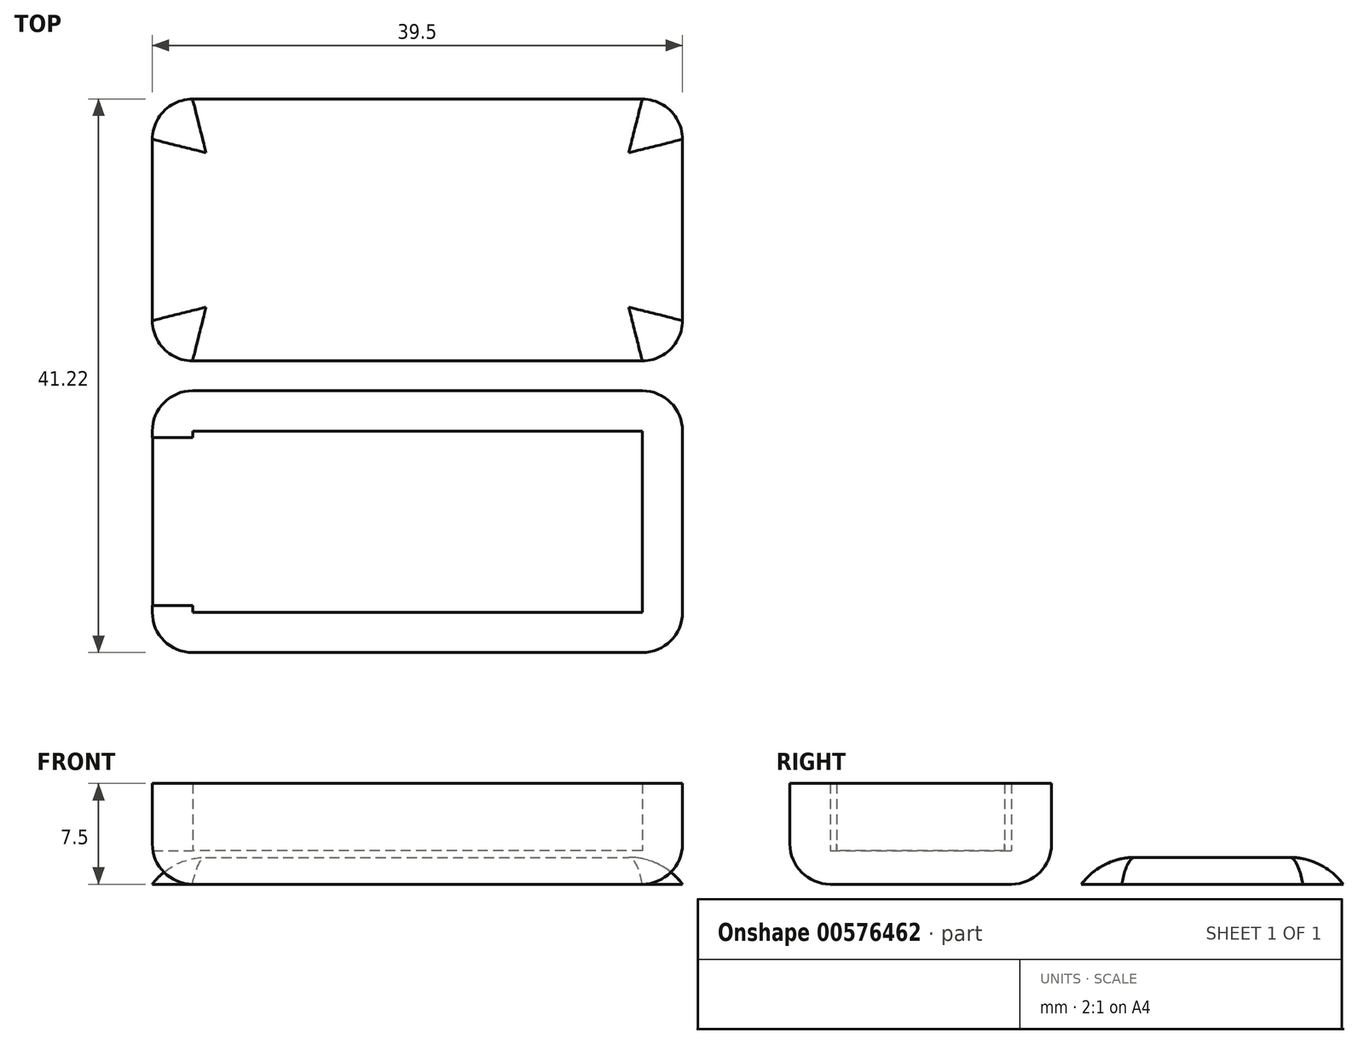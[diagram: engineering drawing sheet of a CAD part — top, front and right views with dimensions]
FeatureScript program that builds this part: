
annotation { "Feature Type Name" : "Feature", "Feature Type Description" : "" }
export const myFeature = defineFeature(function(context is Context, id is Id, definition is map)
    precondition{}
    {
        {
            var Q0;
            Q0=qCreatedBy(makeId("Top.planeOp"),FACE);
            var sketch = newSketch(context, id + "F0", { "sketchPlane" : qUnion([Q0])});
            skLineSegment(sketch, "E0.bottom", {"start": v(16.75, -6.75) * mm, "end": v(-16.75, -6.75) * mm});
            skLineSegment(sketch, "E0.top", {"start": v(16.75, 6.75) * mm, "end": v(-16.75, 6.75) * mm});
            skLineSegment(sketch, "E0.left", {"start": v(16.75, -6.75) * mm, "end": v(16.75, 6.75) * mm});
            skLineSegment(sketch, "E0.right", {"start": v(-16.75, -6.75) * mm, "end": v(-16.75, 6.75) * mm});
            skPoint(sketch, "E0.middle", {"position": v(0, 0) * mm});
            skLineSegment(sketch, "E1.0", {"start": v(16.75, 9.75) * mm, "end": v(-16.75, 9.75) * mm});
            skLineSegment(sketch, "E1.1", {"start": v(19.75, -6.75) * mm, "end": v(19.75, 6.75) * mm});
            skLineSegment(sketch, "E1.2", {"start": v(16.75, -9.75) * mm, "end": v(-16.75, -9.75) * mm});
            skLineSegment(sketch, "E1.3", {"start": v(-19.75, -6.75) * mm, "end": v(-19.75, 6.75) * mm});
            skLineSegment(sketch, "E2.bottom", {"start": v(-19.75, 6.25) * mm, "end": v(-16.75, 6.25) * mm});
            skLineSegment(sketch, "E2.top", {"start": v(-19.75, -6.25) * mm, "end": v(-16.75, -6.25) * mm});
            skLineSegment(sketch, "E2.left", {"start": v(-19.75, 6.25) * mm, "end": v(-19.75, -6.25) * mm});
            skLineSegment(sketch, "E2.right", {"start": v(-16.75, 6.25) * mm, "end": v(-16.75, -6.25) * mm});
            skPoint(sketch, "E3.visualSharp", {"position": v(-19.75, 9.75) * mm});
            skArc(sketch, "E3.filletArc", {"start": v(-16.75, 9.75) * mm, "mid": v(-18.87, 8.87) * mm, "end": v(-19.75, 6.75) * mm});
            skPoint(sketch, "E4.visualSharp", {"position": v(19.75, 9.75) * mm});
            skArc(sketch, "E4.filletArc", {"start": v(19.75, 6.75) * mm, "mid": v(18.87, 8.87) * mm, "end": v(16.75, 9.75) * mm});
            skPoint(sketch, "E5.visualSharp", {"position": v(19.75, -9.75) * mm});
            skArc(sketch, "E5.filletArc", {"start": v(16.75, -9.75) * mm, "mid": v(18.87, -8.87) * mm, "end": v(19.75, -6.75) * mm});
            skPoint(sketch, "E6.visualSharp", {"position": v(-19.75, -9.75) * mm});
            skArc(sketch, "E6.filletArc", {"start": v(-19.75, -6.75) * mm, "mid": v(-18.87, -8.87) * mm, "end": v(-16.75, -9.75) * mm});
            skSolve(sketch);
        }
        {
            var Q0;
            {var subQ1=sQuery(id+"F0.wireOp",EDGE,"E0.bottom");Q0=makeQuery(id+"F0.imprint","IMPRINT",FACE,{"disambiguationData":[TD([[makeQuery(id+"F0.imprint","IMPRINT",EDGE,{"derivedFrom":subQ1}),-1.0]])]});}
            var Q1;
            Q1=makeQuery(id+"F0.imprint","IMPRINT",FACE,{"disambiguationData":[TD([[makeQuery(id+"F0.imprint","IMPRINT",EDGE,{"derivedFrom":sQuery(id+"F0.wireOp",EDGE,"E2.bottom")}),-1.0]])]});
            extrude(context, id + "F1", {"entities" : qUnion([Q0, Q1]), "depth" : 2.5 * mm, "offsetDistance" : 25 * mm});
        }
        {
            var Q0;
            Q0=qCreatedBy(makeId("Top.planeOp"),FACE);
            var sketch = newSketch(context, id + "F2", { "sketchPlane" : qUnion([Q0])});
            skLineSegment(sketch, "E7.bottom", {"start": v(16.75, -6.75) * mm, "end": v(-16.75, -6.75) * mm});
            skLineSegment(sketch, "E7.top", {"start": v(16.75, 6.75) * mm, "end": v(-16.75, 6.75) * mm});
            skLineSegment(sketch, "E7.left", {"start": v(16.75, -6.75) * mm, "end": v(16.75, 6.75) * mm});
            skLineSegment(sketch, "E7.right", {"start": v(-16.75, -6.75) * mm, "end": v(-16.75, 6.75) * mm});
            skPoint(sketch, "E7.middle", {"position": v(0, 0) * mm});
            skLineSegment(sketch, "E8.0", {"start": v(16.75, 9.75) * mm, "end": v(-16.75, 9.75) * mm});
            skLineSegment(sketch, "E8.1", {"start": v(19.75, -6.75) * mm, "end": v(19.75, 6.75) * mm});
            skLineSegment(sketch, "E8.2", {"start": v(16.75, -9.75) * mm, "end": v(-16.75, -9.75) * mm});
            skLineSegment(sketch, "E8.3", {"start": v(-19.75, -6.75) * mm, "end": v(-19.75, 6.75) * mm});
            skLineSegment(sketch, "E9.bottom", {"start": v(-19.75, 6.25) * mm, "end": v(-16.75, 6.25) * mm});
            skLineSegment(sketch, "E9.top", {"start": v(-19.75, -6.25) * mm, "end": v(-16.75, -6.25) * mm});
            skLineSegment(sketch, "E9.left", {"start": v(-19.75, 6.25) * mm, "end": v(-19.75, -6.25) * mm});
            skLineSegment(sketch, "E9.right", {"start": v(-16.75, 6.25) * mm, "end": v(-16.75, -6.25) * mm});
            skPoint(sketch, "E10.visualSharp", {"position": v(-19.75, 9.75) * mm});
            skArc(sketch, "E10.filletArc", {"start": v(-16.75, 9.75) * mm, "mid": v(-18.87, 8.87) * mm, "end": v(-19.75, 6.75) * mm});
            skPoint(sketch, "E11.visualSharp", {"position": v(19.75, 9.75) * mm});
            skArc(sketch, "E11.filletArc", {"start": v(19.75, 6.75) * mm, "mid": v(18.87, 8.87) * mm, "end": v(16.75, 9.75) * mm});
            skPoint(sketch, "E12.visualSharp", {"position": v(19.75, -9.75) * mm});
            skArc(sketch, "E12.filletArc", {"start": v(16.75, -9.75) * mm, "mid": v(18.87, -8.87) * mm, "end": v(19.75, -6.75) * mm});
            skPoint(sketch, "E13.visualSharp", {"position": v(-19.75, -9.75) * mm});
            skArc(sketch, "E13.filletArc", {"start": v(-19.75, -6.75) * mm, "mid": v(-18.87, -8.87) * mm, "end": v(-16.75, -9.75) * mm});
            skSolve(sketch);
        }
        {
            var Q0;
            {var subQ9=sQuery(id+"F2.wireOp",EDGE,"E7.bottom");Q0=makeQuery(id+"F2.imprint","IMPRINT",FACE,{"disambiguationData":[TD([[makeQuery(id+"F2.imprint","IMPRINT",EDGE,{"derivedFrom":subQ9}),1.0]])]});}
            extrude(context, id + "F3", {"entities" : qUnion([Q0]), "operationType" : NewBodyOperationType.ADD, "depth" : 7.5 * mm, "offsetDistance" : 25 * mm});
        }
        {
            var Q0;
            Q0=qCreatedBy(makeId("Top.planeOp"),FACE);
            var sketch = newSketch(context, id + "F4", { "sketchPlane" : qUnion([Q0])});
            skPoint(sketch, "E14.middle", {"position": v(0, 21.72) * mm});
            skLineSegment(sketch, "E15.0", {"start": v(16.75, 31.47) * mm, "end": v(-16.75, 31.47) * mm});
            skLineSegment(sketch, "E15.1", {"start": v(19.75, 14.97) * mm, "end": v(19.75, 28.47) * mm});
            skLineSegment(sketch, "E15.2", {"start": v(16.75, 11.97) * mm, "end": v(-16.75, 11.97) * mm});
            skLineSegment(sketch, "E15.3", {"start": v(-19.75, 14.97) * mm, "end": v(-19.75, 28.47) * mm});
            skLineSegment(sketch, "E16.left", {"start": v(-19.75, 27.97) * mm, "end": v(-19.75, 15.47) * mm});
            skPoint(sketch, "E17.visualSharp", {"position": v(-19.75, 31.47) * mm});
            skArc(sketch, "E17.filletArc", {"start": v(-16.75, 31.47) * mm, "mid": v(-18.87, 30.6) * mm, "end": v(-19.75, 28.47) * mm});
            skPoint(sketch, "E18.visualSharp", {"position": v(19.75, 31.47) * mm});
            skArc(sketch, "E18.filletArc", {"start": v(19.75, 28.47) * mm, "mid": v(18.87, 30.6) * mm, "end": v(16.75, 31.47) * mm});
            skPoint(sketch, "E19.visualSharp", {"position": v(19.75, 11.97) * mm});
            skArc(sketch, "E19.filletArc", {"start": v(16.75, 11.97) * mm, "mid": v(18.87, 12.85) * mm, "end": v(19.75, 14.97) * mm});
            skPoint(sketch, "E20.visualSharp", {"position": v(-19.75, 11.97) * mm});
            skArc(sketch, "E20.filletArc", {"start": v(-19.75, 14.97) * mm, "mid": v(-18.87, 12.85) * mm, "end": v(-16.75, 11.97) * mm});
            skSolve(sketch);
        }
        {
            var Q0;
            Q0=makeQuery(id+"F4.imprint","IMPRINT",FACE,{"disambiguationData":[TD([[makeQuery(id+"F4.imprint","IMPRINT",EDGE,{"derivedFrom":sQuery(id+"F4.wireOp",EDGE,"E15.0")}),1.0]])]});
            extrude(context, id + "F5", {"entities" : qUnion([Q0]), "depth" : 2 * mm, "offsetDistance" : 25 * mm});
        }
        {
            var Q0;
            Q0=makeQuery(id+"F3.opExtrude","CAP_EDGE",EDGE,{"disambiguationData":[OSD([sQuery(id+"F2.wireOp",EDGE,"E13.filletArc")])],"isStart":true});
            fillet(context, id + "F6", {"entities" : qUnion([Q0]), "radius" : 3 * mm, "tangentPropagation" : true, "allowEdgeOverflow" : false});
        }
        {
            var Q0;
            Q0=makeQuery(id+"F5.opExtrude","CAP_FACE",FACE,{"disambiguationData":[OSD([sQuery(id+"F4.wireOp",EDGE,"E15.0"),sQuery(id+"F4.wireOp",EDGE,"E15.1"),sQuery(id+"F4.wireOp",EDGE,"E15.2"),sQuery(id+"F4.wireOp",EDGE,"E15.3"),sQuery(id+"F4.wireOp",EDGE,"E16.left"),sQuery(id+"F4.wireOp",EDGE,"E17.filletArc"),sQuery(id+"F4.wireOp",EDGE,"E18.filletArc"),sQuery(id+"F4.wireOp",EDGE,"E19.filletArc"),sQuery(id+"F4.wireOp",EDGE,"E20.filletArc")])],"isStart":false});
            fillet(context, id + "F7", {"entities" : qUnion([Q0]), "radius" : 5 * mm, "tangentPropagation" : true, "allowEdgeOverflow" : false});
        }
    });
